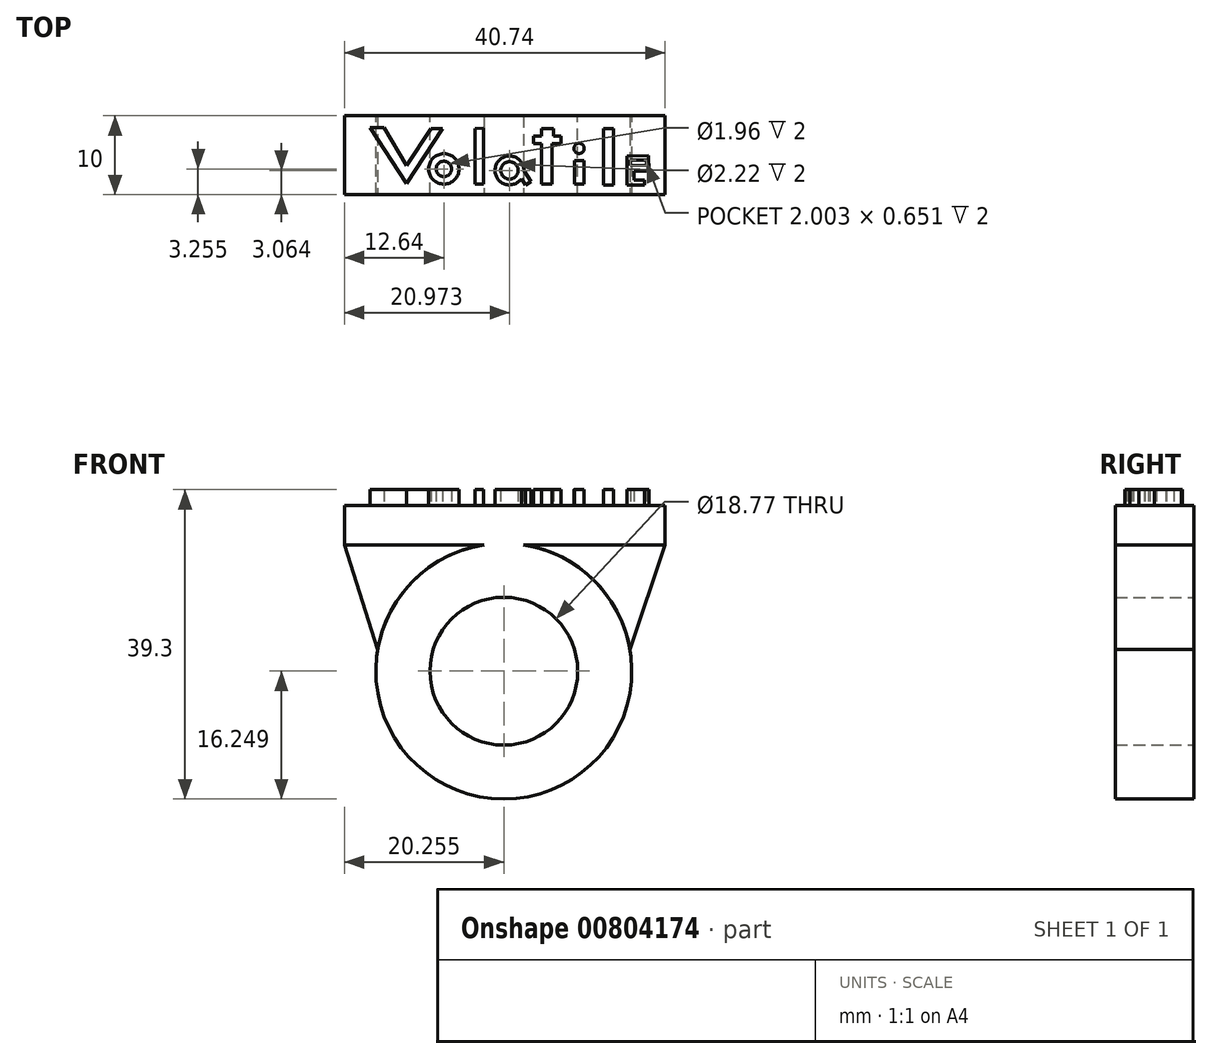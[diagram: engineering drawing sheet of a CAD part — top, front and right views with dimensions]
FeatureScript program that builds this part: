
annotation { "Feature Type Name" : "Feature", "Feature Type Description" : "" }
export const myFeature = defineFeature(function(context is Context, id is Id, definition is map)
    precondition{}
    {
        {
            var Q0;
            Q0=qCreatedBy(makeId("Front.planeOp"),FACE);
            var sketch = newSketch(context, id + "F0", { "sketchPlane" : qUnion([Q0])});
            skCircle(sketch, "E0", {"center": v(-13.1, 7.34) * mm, "radius": 9.38 * mm});
            skCircle(sketch, "E1", {"center": v(-13.1, 7.34) * mm, "radius": 16.25 * mm});
            skSolve(sketch);
        }
        {
            var Q0;
            Q0 = qSketchRegion(id + "F0", true);
            extrude(context, id + "F1", {"entities" : qUnion([Q0]), "depth" : 10 * mm, "offsetDistance" : 25 * mm});
        }
        {
            var Q0;
            Q0=makeQuery(id+"F1.opExtrude","CAP_FACE",FACE,{"disambiguationData":[OSD([sQuery(id+"F0.wireOp",EDGE,"E0"),sQuery(id+"F0.wireOp",EDGE,"E1")])],"isStart":false});
            var sketch = newSketch(context, id + "F2", { "sketchPlane" : qUnion([Q0])});
            skLineSegment(sketch, "E2", {"start": v(-33.35, 23.4) * mm, "end": v(-33.35, 28.4) * mm});
            skLineSegment(sketch, "E3", {"start": v(7.4, 23.4) * mm, "end": v(7.4, 28.4) * mm});
            skLineSegment(sketch, "E4", {"start": v(-33.35, 28.4) * mm, "end": v(7.4, 28.4) * mm});
            skLineSegment(sketch, "E5", {"start": v(-33.35, 23.4) * mm, "end": v(7.4, 23.4) * mm});
            skSolve(sketch);
        }
        {
            var Q0;
            Q0 = qSketchRegion(id + "F2", true);
            extrude(context, id + "F3", {"entities" : qUnion([Q0]), "operationType" : NewBodyOperationType.ADD, "oppositeDirection" : true, "depth" : 10 * mm, "offsetDistance" : 25 * mm});
        }
        {
            var Q0;
            Q0=makeQuery(id+"F3.opExtrude","SWEPT_FACE",FACE,{"disambiguationData":[OSD([sQuery(id+"F2.wireOp",EDGE,"E4")])]});
            var sketch = newSketch(context, id + "F4", { "sketchPlane" : qUnion([Q0])});
            skLineSegment(sketch, "E6", {"start": v(-30.1, -1.5) * mm, "end": v(-28.33, -1.5) * mm});
            skLineSegment(sketch, "E7", {"start": v(-28.33, -1.5) * mm, "end": v(-25.47, -6.32) * mm});
            skLineSegment(sketch, "E8", {"start": v(-25.47, -6.32) * mm, "end": v(-22.33, -1.6) * mm});
            skLineSegment(sketch, "E9", {"start": v(-22.33, -1.6) * mm, "end": v(-20.85, -1.6) * mm});
            skLineSegment(sketch, "E10", {"start": v(-20.85, -1.6) * mm, "end": v(-25.47, -8.6) * mm});
            skLineSegment(sketch, "E11", {"start": v(-25.47, -8.6) * mm, "end": v(-30.1, -1.5) * mm});
            skPoint(sketch, "E12.end.orphan", {"position": v(-13.76, -1.6) * mm});
            skPoint(sketch, "E13.end.orphan", {"position": v(-12.42, -1.6) * mm});
            skCircle(sketch, "E14", {"center": v(-20.71, -6.75) * mm, "radius": 1.93 * mm});
            skCircle(sketch, "E15", {"center": v(-20.71, -6.75) * mm, "radius": 0.98 * mm});
            skLineSegment(sketch, "E16", {"start": v(-16.76, -1.6) * mm, "end": v(-16.76, -8.7) * mm});
            skLineSegment(sketch, "E17", {"start": v(-16.76, -8.7) * mm, "end": v(-15.66, -8.7) * mm});
            skLineSegment(sketch, "E18", {"start": v(-15.66, -8.7) * mm, "end": v(-15.66, -1.55) * mm});
            skLineSegment(sketch, "E19", {"start": v(-15.66, -1.55) * mm, "end": v(-16.76, -1.6) * mm});
            skCircle(sketch, "E20", {"center": v(-12.38, -6.94) * mm, "radius": 1.84 * mm});
            skCircle(sketch, "E21", {"center": v(-12.38, -6.94) * mm, "radius": 1.11 * mm});
            skLineSegment(sketch, "E22", {"start": v(-10.54, -6.94) * mm, "end": v(-9.66, -8.36) * mm});
            skLineSegment(sketch, "E23", {"start": v(-9.66, -8.36) * mm, "end": v(-10.33, -8.77) * mm});
            skLineSegment(sketch, "E24", {"start": v(-10.33, -8.77) * mm, "end": v(-10.84, -7.94) * mm});
            skLineSegment(sketch, "E25", {"start": v(-8.34, -1.6) * mm, "end": v(-8.34, -2.55) * mm});
            skLineSegment(sketch, "E26", {"start": v(-8.34, -8.7) * mm, "end": v(-7, -8.7) * mm});
            skLineSegment(sketch, "E27", {"start": v(-7, -8.7) * mm, "end": v(-7, -3.55) * mm});
            skLineSegment(sketch, "E28", {"start": v(-7, -3.55) * mm, "end": v(-5.8, -3.55) * mm});
            skLineSegment(sketch, "E29", {"start": v(-5.8, -3.55) * mm, "end": v(-5.8, -2.55) * mm});
            skLineSegment(sketch, "E30", {"start": v(-5.8, -2.55) * mm, "end": v(-6.8, -2.55) * mm});
            skLineSegment(sketch, "E31", {"start": v(-6.8, -2.55) * mm, "end": v(-6.8, -1.6) * mm});
            skLineSegment(sketch, "E32", {"start": v(-8.34, -1.6) * mm, "end": v(-6.8, -1.6) * mm});
            skLineSegment(sketch, "E33", {"start": v(-8.34, -3.55) * mm, "end": v(-8.34, -8.7) * mm});
            skLineSegment(sketch, "E34", {"start": v(-8.34, -2.55) * mm, "end": v(-9.34, -2.55) * mm});
            skLineSegment(sketch, "E35", {"start": v(-9.34, -2.55) * mm, "end": v(-9.34, -3.55) * mm});
            skLineSegment(sketch, "E36", {"start": v(-9.34, -3.55) * mm, "end": v(-8.34, -3.55) * mm});
            skLineSegment(sketch, "E37", {"start": v(-4.09, -8.7) * mm, "end": v(-4.09, -5.7) * mm});
            skLineSegment(sketch, "E38", {"start": v(-4.09, -5.7) * mm, "end": v(-2.89, -5.7) * mm});
            skLineSegment(sketch, "E39", {"start": v(-2.89, -5.7) * mm, "end": v(-2.89, -8.7) * mm});
            skLineSegment(sketch, "E40", {"start": v(-2.89, -8.7) * mm, "end": v(-4.09, -8.7) * mm});
            skCircle(sketch, "E41", {"center": v(-3.54, -4.14) * mm, "radius": 0.65 * mm});
            skLineSegment(sketch, "E42", {"start": v(-0.43, -1.6) * mm, "end": v(-0.43, -8.8) * mm});
            skLineSegment(sketch, "E43", {"start": v(-0.43, -8.8) * mm, "end": v(0.82, -8.8) * mm});
            skLineSegment(sketch, "E44", {"start": v(0.82, -8.8) * mm, "end": v(0.82, -1.6) * mm});
            skLineSegment(sketch, "E45", {"start": v(0.82, -1.6) * mm, "end": v(-0.43, -1.6) * mm});
            skPoint(sketch, "E46.1.internal.orphan", {"position": v(5.27, -5.04) * mm});
            skPoint(sketch, "E46.2.internal.orphan", {"position": v(5.27, -4.29) * mm});
            skPoint(sketch, "E47.end.orphan", {"position": v(3.02, -4.64) * mm});
            skPoint(sketch, "E48.orphan", {"position": v(3.02, -5.64) * mm});
            skPoint(sketch, "E49.start.orphan", {"position": v(3.02, -4.29) * mm});
            skPoint(sketch, "E50.orphan", {"position": v(5.27, -5.64) * mm});
            skPoint(sketch, "E51.start.orphan", {"position": v(3.02, -6.3) * mm});
            skPoint(sketch, "E52.start.orphan", {"position": v(5.47, -8.8) * mm});
            skPoint(sketch, "E53.start.orphan", {"position": v(5.02, -5.64) * mm});
            skLineSegment(sketch, "E54", {"start": v(4.77, -8.8) * mm, "end": v(4.77, -8.15) * mm});
            skLineSegment(sketch, "E55", {"start": v(4.77, -8.15) * mm, "end": v(3.42, -8.15) * mm});
            skLineSegment(sketch, "E56", {"start": v(3.42, -8.15) * mm, "end": v(3.42, -7) * mm});
            skLineSegment(sketch, "E57", {"start": v(3.42, -7) * mm, "end": v(5.32, -7) * mm});
            skLineSegment(sketch, "E58", {"start": v(5.32, -7) * mm, "end": v(5.27, -5.04) * mm});
            skLineSegment(sketch, "E59", {"start": v(5.27, -5.04) * mm, "end": v(2.57, -5.11) * mm});
            skLineSegment(sketch, "E60", {"start": v(2.57, -5.11) * mm, "end": v(2.57, -8.8) * mm});
            skPoint(sketch, "E61.start.orphan", {"position": v(2.87, -8.8) * mm});
            skLineSegment(sketch, "E62", {"start": v(2.57, -8.8) * mm, "end": v(4.77, -8.8) * mm});
            skLineSegment(sketch, "E63", {"start": v(3.02, -5.64) * mm, "end": v(5.02, -5.64) * mm});
            skLineSegment(sketch, "E64", {"start": v(3.02, -5.64) * mm, "end": v(3.02, -6.3) * mm});
            skLineSegment(sketch, "E65", {"start": v(3.02, -6.3) * mm, "end": v(5.02, -6.24) * mm});
            skLineSegment(sketch, "E66", {"start": v(5.02, -6.24) * mm, "end": v(5.02, -5.64) * mm});
            skSolve(sketch);
        }
        {
            var Q0;
            Q0 = qSketchRegion(id + "F4", true);
            extrude(context, id + "F5", {"entities" : qUnion([Q0]), "operationType" : NewBodyOperationType.ADD, "depth" : 2 * mm, "offsetDistance" : 25 * mm});
        }
        {
            var Q0;
            Q0=makeQuery(id+"F3.boolean.opBoolean","MERGE",FACE,{"derivedFrom":[makeQuery(id+"F1.opExtrude","CAP_FACE",FACE,{"disambiguationData":[OSD([sQuery(id+"F0.wireOp",EDGE,"E0"),sQuery(id+"F0.wireOp",EDGE,"E1")])],"isStart":false}),makeQuery(id+"F3.opExtrude","CAP_FACE",FACE,{"disambiguationData":[OSD([sQuery(id+"F2.wireOp",EDGE,"E2"),sQuery(id+"F2.wireOp",EDGE,"E3"),sQuery(id+"F2.wireOp",EDGE,"E4"),sQuery(id+"F2.wireOp",EDGE,"E5")])],"isStart":true})]});
            var sketch = newSketch(context, id + "F6", { "sketchPlane" : qUnion([Q0])});
            skLineSegment(sketch, "E67", {"start": v(-33.35, 23.4) * mm, "end": v(-29.1, 10.1) * mm});
            skLineSegment(sketch, "E68", {"start": v(2.92, 10.1) * mm, "end": v(7.4, 23.4) * mm});
            skSolve(sketch);
        }
        {
            var Q0;
            Q0 = qSketchRegion(id + "F6", true);
            var Q1;
            {var subQ0=sQuery(id+"F6.wireOp",EDGE,"E67");Q1=makeQuery(id+"F6.imprint","IMPRINT",FACE,{"disambiguationData":[TD([[makeQuery(id+"F6.imprint","IMPRINT",EDGE,{"derivedFrom":subQ0}),1.0]])]});}
            var Q2;
            {var subQ0=sQuery(id+"F6.wireOp",EDGE,"E68");Q2=makeQuery(id+"F6.imprint","IMPRINT",FACE,{"disambiguationData":[TD([[makeQuery(id+"F6.imprint","IMPRINT",EDGE,{"derivedFrom":subQ0}),1.0]])]});}
            extrude(context, id + "F7", {"entities" : qUnion([Q0, Q1, Q2]), "oppositeDirection" : true, "depth" : 10 * mm, "offsetDistance" : 25 * mm});
        }
    });
